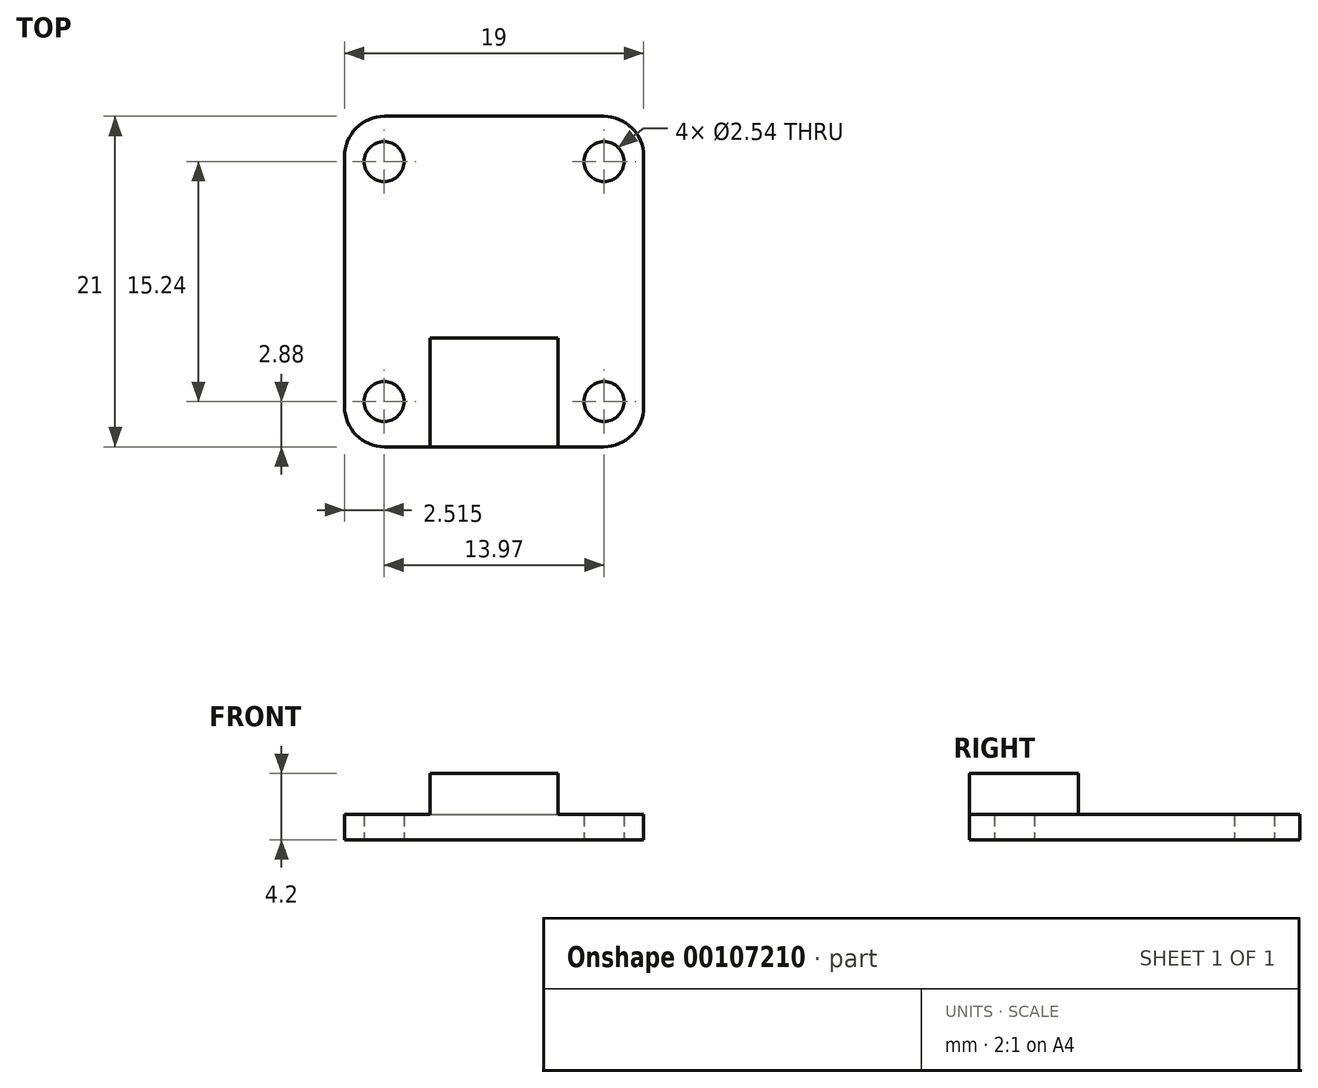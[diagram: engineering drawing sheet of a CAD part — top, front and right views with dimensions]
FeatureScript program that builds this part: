
annotation { "Feature Type Name" : "Feature", "Feature Type Description" : "" }
export const myFeature = defineFeature(function(context is Context, id is Id, definition is map)
    precondition{}
    {
        {
            var Q0;
            Q0=qCreatedBy(makeId("Top.planeOp"),FACE);
            var sketch = newSketch(context, id + "F0", { "sketchPlane" : qUnion([Q0])});
            skLineSegment(sketch, "E0.bottom", {"start": v(2.54, 0) * mm, "end": v(16.46, 0) * mm});
            skLineSegment(sketch, "E0.top", {"start": v(2.54, 21) * mm, "end": v(16.46, 21) * mm});
            skLineSegment(sketch, "E0.left", {"start": v(0, 2.54) * mm, "end": v(0, 18.46) * mm});
            skLineSegment(sketch, "E0.right", {"start": v(19, 2.54) * mm, "end": v(19, 18.46) * mm});
            skLineSegment(sketch, "E1.bottom", {"start": v(2.52, 2.88) * mm, "end": v(16.48, 2.88) * mm, "construction": true});
            skLineSegment(sketch, "E1.top", {"start": v(2.52, 18.12) * mm, "end": v(16.48, 18.12) * mm, "construction": true});
            skLineSegment(sketch, "E1.left", {"start": v(2.51, 2.88) * mm, "end": v(2.51, 18.12) * mm, "construction": true});
            skLineSegment(sketch, "E1.right", {"start": v(16.49, 2.88) * mm, "end": v(16.49, 18.12) * mm, "construction": true});
            skLineSegment(sketch, "E2", {"start": v(9.5, 18.12) * mm, "end": v(9.5, 21) * mm, "construction": true});
            skLineSegment(sketch, "E3", {"start": v(16.49, 10.5) * mm, "end": v(19, 10.5) * mm, "construction": true});
            skCircle(sketch, "E4", {"center": v(2.52, 18.12) * mm, "radius": 1.27 * mm});
            skCircle(sketch, "E5", {"center": v(2.52, 2.88) * mm, "radius": 1.27 * mm});
            skCircle(sketch, "E6", {"center": v(16.48, 2.88) * mm, "radius": 1.27 * mm});
            skCircle(sketch, "E7", {"center": v(16.48, 18.12) * mm, "radius": 1.27 * mm});
            skPoint(sketch, "E8.visualSharp", {"position": v(0, 21) * mm});
            skArc(sketch, "E8.filletArc", {"start": v(2.54, 21) * mm, "mid": v(0.74, 20.26) * mm, "end": v(0, 18.46) * mm});
            skPoint(sketch, "E9.visualSharp", {"position": v(19, 21) * mm});
            skArc(sketch, "E9.filletArc", {"start": v(19, 18.46) * mm, "mid": v(18.26, 20.26) * mm, "end": v(16.46, 21) * mm});
            skPoint(sketch, "E10.visualSharp", {"position": v(19, 0) * mm});
            skArc(sketch, "E10.filletArc", {"start": v(16.46, 0) * mm, "mid": v(18.26, 0.74) * mm, "end": v(19, 2.54) * mm});
            skPoint(sketch, "E11.visualSharp", {"position": v(0, 0) * mm});
            skArc(sketch, "E11.filletArc", {"start": v(0, 2.54) * mm, "mid": v(0.74, 0.74) * mm, "end": v(2.54, 0) * mm});
            skSolve(sketch);
        }
        {
            var Q0;
            Q0=makeQuery(id+"F0.imprint","IMPRINT",FACE,{"disambiguationData":[TD([[makeQuery(id+"F0.imprint","IMPRINT",EDGE,{"derivedFrom":sQuery(id+"F0.wireOp",EDGE,"E0.bottom")}),1.0]])]});
            extrude(context, id + "F1", {"entities" : qUnion([Q0]), "depth" : 1.6 * mm});
        }
        {
            var Q0;
            Q0=makeQuery(id+"F1.opExtrude","CAP_FACE",FACE,{"disambiguationData":[OSD([sQuery(id+"F0.wireOp",EDGE,"E0.bottom"),sQuery(id+"F0.wireOp",EDGE,"E0.top"),sQuery(id+"F0.wireOp",EDGE,"E0.left"),sQuery(id+"F0.wireOp",EDGE,"E0.right"),sQuery(id+"F0.wireOp",EDGE,"E4"),sQuery(id+"F0.wireOp",EDGE,"E5"),sQuery(id+"F0.wireOp",EDGE,"E6"),sQuery(id+"F0.wireOp",EDGE,"E7"),sQuery(id+"F0.wireOp",EDGE,"E8.filletArc"),sQuery(id+"F0.wireOp",EDGE,"E9.filletArc"),sQuery(id+"F0.wireOp",EDGE,"E10.filletArc"),sQuery(id+"F0.wireOp",EDGE,"E11.filletArc")])],"isStart":false});
            var sketch = newSketch(context, id + "F2", { "sketchPlane" : qUnion([Q0])});
            skLineSegment(sketch, "E12.bottom", {"start": v(5.44, 0) * mm, "end": v(13.56, 0) * mm});
            skLineSegment(sketch, "E12.top", {"start": v(5.44, 6.92) * mm, "end": v(13.56, 6.92) * mm});
            skLineSegment(sketch, "E12.left", {"start": v(5.44, 0) * mm, "end": v(5.44, 6.92) * mm});
            skLineSegment(sketch, "E12.right", {"start": v(13.56, 0) * mm, "end": v(13.56, 6.92) * mm});
            skPoint(sketch, "E13", {"position": v(9.5, 0) * mm});
            skSolve(sketch);
        }
        {
            var Q0;
            Q0=makeQuery(id+"F2.imprint","IMPRINT",FACE,{"disambiguationData":[TD([[makeQuery(id+"F2.imprint","IMPRINT",EDGE,{"derivedFrom":sQuery(id+"F2.wireOp",EDGE,"E12.bottom")}),1.0]])]});
            extrude(context, id + "F3", {"entities" : qUnion([Q0]), "operationType" : NewBodyOperationType.ADD, "depth" : 2.6 * mm});
        }
    });
